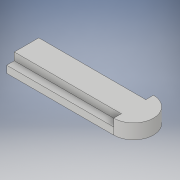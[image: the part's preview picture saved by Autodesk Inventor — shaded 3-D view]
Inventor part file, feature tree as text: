
AUTODESK INVENTOR PART (.ipt)
format: ipt  version: 2019 (Build 230136000, 136)  size: 111,616 bytes
history: native  units: in
note: dims shown in document units (in); Inventor stores cm internally (conversion verified against a paired STEP export)
features: extrude x2, sketch x2
ambient origin geometry x8: Origin, YZ Plane, XZ Plane, XY Plane, X Axis, Y Axis, Z Axis, Center Point
bodies: Solid1 (feature_tree)
feature tree (4):
  extrude  "Extrusion1"  Depth=0.4in
  extrude  "Extrusion2"  Depth=0.115in
  sketch  "Sketch1"  dims[d0=0.65in d1=0.4in]
  sketch  "Sketch2"  dims[d2=0.125in d3=0.115in d4=0.125in d5=1.75in d6=0.0in d7=0.75in d8=0.0in]
